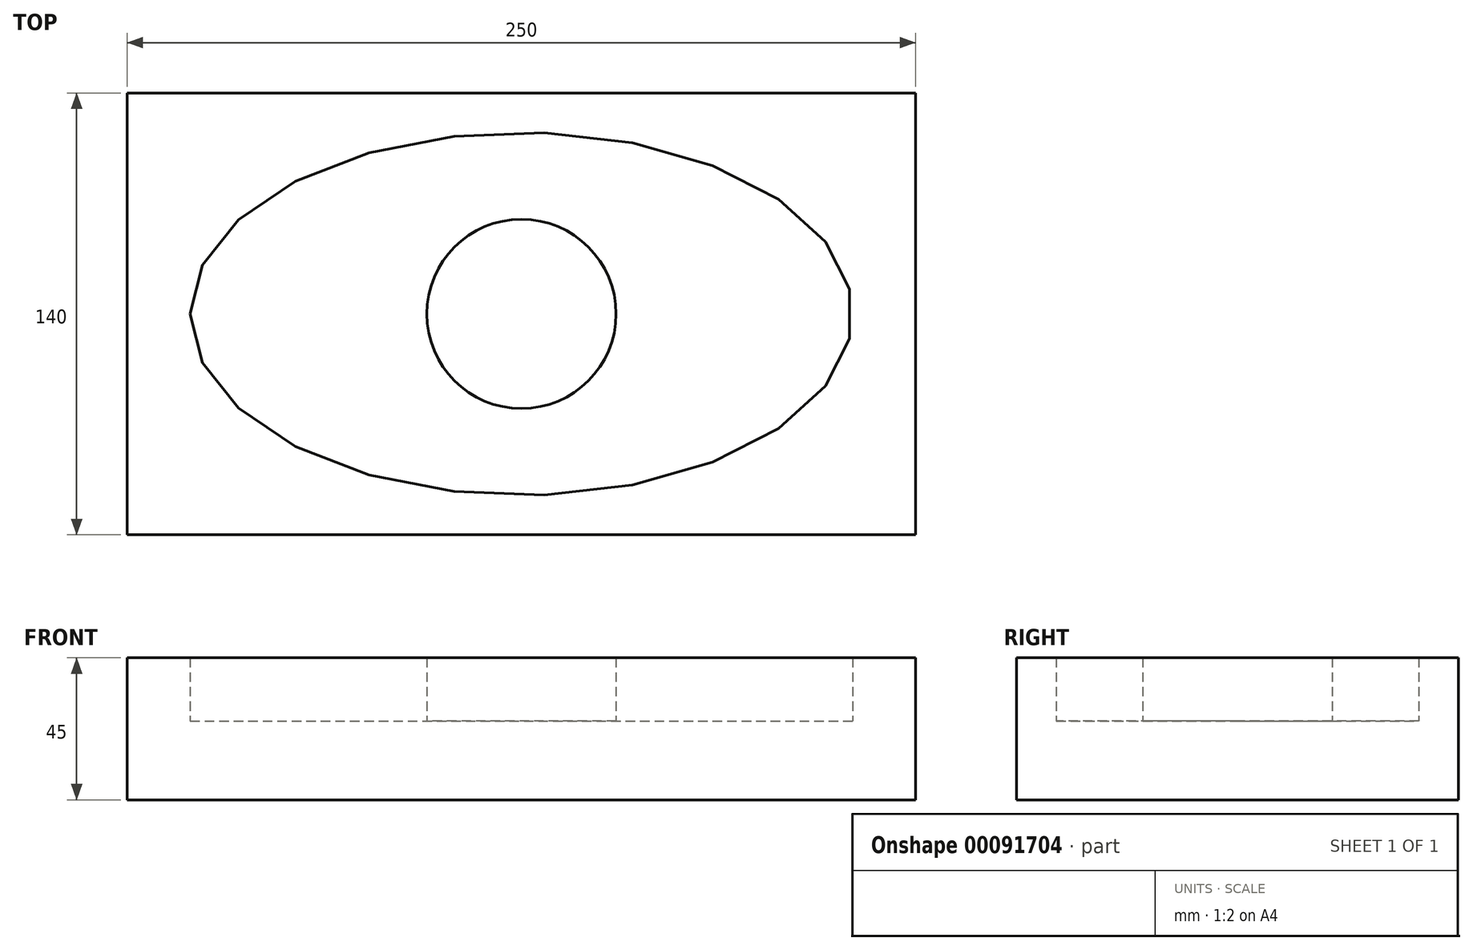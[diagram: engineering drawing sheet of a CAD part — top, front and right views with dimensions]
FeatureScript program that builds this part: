
annotation { "Feature Type Name" : "Feature", "Feature Type Description" : "" }
export const myFeature = defineFeature(function(context is Context, id is Id, definition is map)
    precondition{}
    {
        {
            var Q0;
            Q0=qCreatedBy(makeId("Front.planeOp"),FACE);
            var sketch = newSketch(context, id + "F0", { "sketchPlane" : qUnion([Q0])});
            skLineSegment(sketch, "E0.bottom", {"start": v(-125, -12.5) * mm, "end": v(125, -12.5) * mm});
            skLineSegment(sketch, "E0.top", {"start": v(-125, 12.5) * mm, "end": v(125, 12.5) * mm});
            skLineSegment(sketch, "E0.left", {"start": v(-125, -12.5) * mm, "end": v(-125, 12.5) * mm});
            skLineSegment(sketch, "E0.right", {"start": v(125, -12.5) * mm, "end": v(125, 12.5) * mm});
            skPoint(sketch, "E0.middle", {"position": v(0, 0) * mm});
            skSolve(sketch);
        }
        {
            var Q0;
            Q0=makeQuery(id+"F0.imprint","IMPRINT",FACE,{"disambiguationData":[TD([[makeQuery(id+"F0.imprint","IMPRINT",EDGE,{"derivedFrom":sQuery(id+"F0.wireOp",EDGE,"E0.bottom")}),1.0]])]});
            extrude(context, id + "F1", {"entities" : qUnion([Q0]), "depth" : 140 * mm});
        }
        {
            var Q0;
            Q0=makeQuery(id+"F1.opExtrude","SWEPT_FACE",FACE,{"disambiguationData":[OSD([sQuery(id+"F0.wireOp",EDGE,"E0.top")])]});
            var sketch = newSketch(context, id + "F2", { "sketchPlane" : qUnion([Q0])});
            skEllipse(sketch, "E1", {"center": v(0, -70) * mm, "majorRadius": 105 * mm, "minorRadius": 57.5 * mm, "majorAxis": v(-1, 0)});
            skPoint(sketch, "E1.centerSnap0", {"position": v(125, -70) * mm});
            skPoint(sketch, "E1.centerSnap1", {"position": v(0, -140) * mm});
            skCircle(sketch, "E2", {"center": v(0, -70) * mm, "radius": 30 * mm});
            skSolve(sketch);
        }
        {
            var Q0;
            Q0=makeQuery(id+"F2.imprint","IMPRINT",FACE,{"disambiguationData":[TD([[makeQuery(id+"F2.imprint","IMPRINT",EDGE,{"derivedFrom":sQuery(id+"F2.wireOp",EDGE,"E1")}),-1.0]])]});
            var Q1;
            Q1=makeQuery(id+"F2.imprint","IMPRINT",FACE,{"disambiguationData":[TD([[makeQuery(id+"F2.imprint","IMPRINT",EDGE,{"derivedFrom":sQuery(id+"F2.wireOp",EDGE,"E2")}),1.0]])]});
            extrude(context, id + "F3", {"entities" : qUnion([Q0, Q1]), "operationType" : NewBodyOperationType.ADD, "depth" : 20 * mm});
        }
    });
